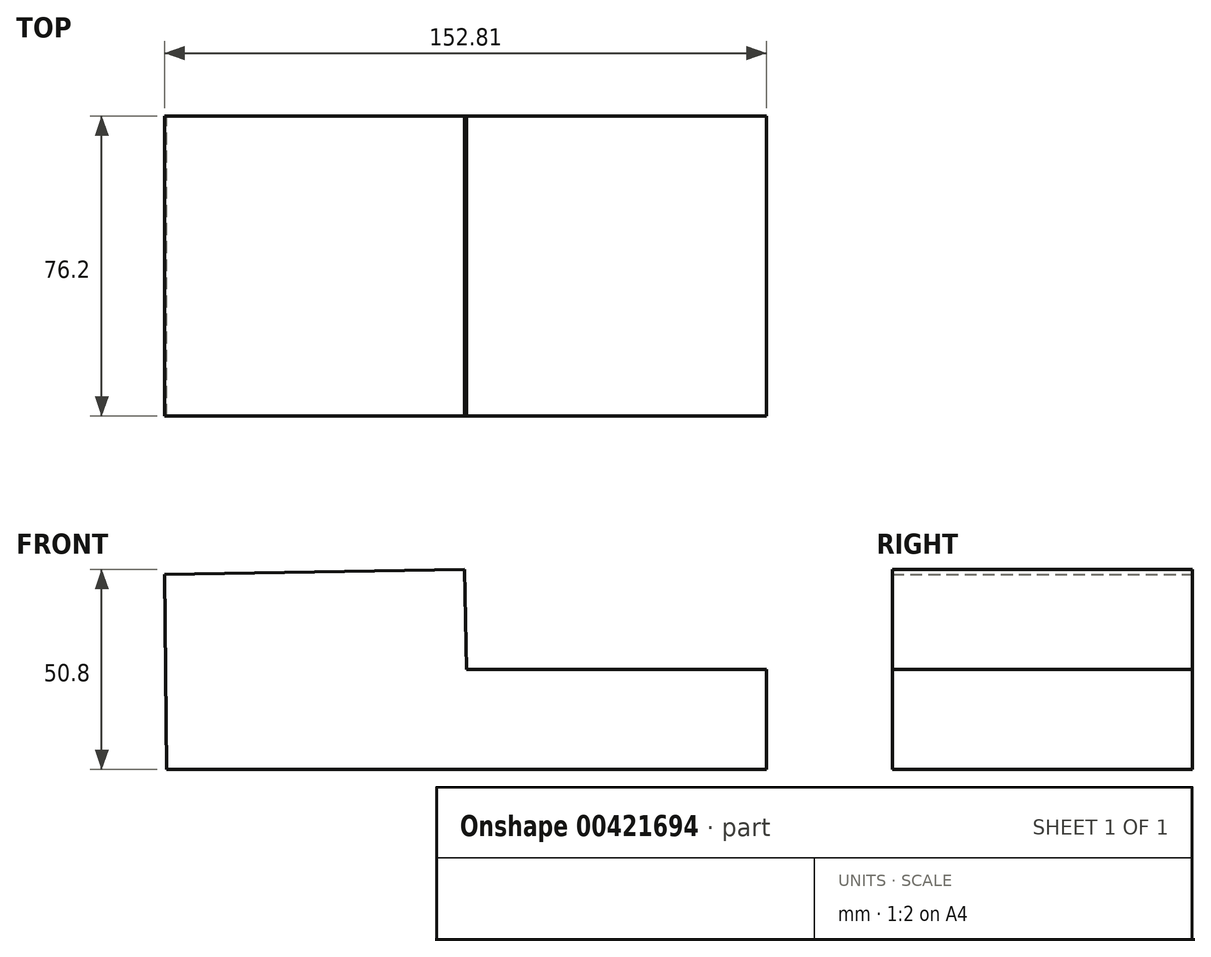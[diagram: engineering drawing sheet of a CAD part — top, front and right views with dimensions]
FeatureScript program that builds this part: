
annotation { "Feature Type Name" : "Feature", "Feature Type Description" : "" }
export const myFeature = defineFeature(function(context is Context, id is Id, definition is map)
    precondition{}
    {
        {
            var Q0;
            Q0=qCreatedBy(makeId("Front.planeOp"),FACE);
            var sketch = newSketch(context, id + "F0", { "sketchPlane" : qUnion([Q0])});
            skLineSegment(sketch, "E0", {"start": v(0, 0) * mm, "end": v(152.4, 0) * mm});
            skLineSegment(sketch, "E1", {"start": v(152.4, 0) * mm, "end": v(152.4, 25.4) * mm});
            skLineSegment(sketch, "E2", {"start": v(152.4, 25.4) * mm, "end": v(76.2, 25.4) * mm});
            skLineSegment(sketch, "E3", {"start": v(76.2, 25.4) * mm, "end": v(75.78, 50.8) * mm});
            skLineSegment(sketch, "E4", {"start": v(75.78, 50.8) * mm, "end": v(-0.4, 49.55) * mm});
            skLineSegment(sketch, "E5", {"start": v(-0.4, 49.55) * mm, "end": v(0, 0) * mm});
            skSolve(sketch);
        }
        {
            var Q0;
            Q0=makeQuery(id+"F0.imprint","IMPRINT",FACE,{"disambiguationData":[TD([[makeQuery(id+"F0.imprint","IMPRINT",EDGE,{"derivedFrom":sQuery(id+"F0.wireOp",EDGE,"E0")}),1.0]])]});
            extrude(context, id + "F1", {"entities" : qUnion([Q0]), "depth" : 76.2 * mm});
        }
    });
